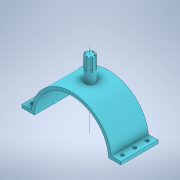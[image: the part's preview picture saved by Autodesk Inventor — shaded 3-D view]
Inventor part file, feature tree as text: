
AUTODESK INVENTOR PART (.ipt)
format: ipt  version: 2021 (Build 250183000, 183)  size: 183,296 bytes
history: native  units: in
note: dims shown in document units (in); Inventor stores cm internally (conversion verified against a paired STEP export)
features: sketch x4, extrude x3, hole x1, mirror x1, plane x1, pattern_circular x1
ambient origin geometry x8: Origin, YZ Plane, XZ Plane, XY Plane, X Axis, Y Axis, Z Axis, Center Point
bodies: Body1 (feature_tree)
feature tree (11):
  extrude  "Extrusion5"  Depth=0.25in
  hole  "Hole3"  [1 undecoded]
  mirror  "Mirror3"
  plane  "Work Plane7"
  extrude  "Extrusion11"  Depth=3.0in TaperAngle=0.0deg
  extrude  "Extrusion12"  Depth=1.0in
  pattern_circular  "Circular Pattern3"  [2 undecoded]
  sketch  "Sketch8"  dims[d52=6.0in d53=0.25in]
  sketch  "Sketch9"  dims[d54=0.75in d55=0.125in]
  sketch  "Sketch20"  dims[d56=0.25in d57=3.0in d58=0.0in]
  sketch  "Sketch21"  dims[d59=0.5in d60=1.1811in d62=1.0in d63=0.3937in d65=1.0in d67=0.266in d68=0.75in d69=0.438in d70=0.25in d71=0.5635in d72=1.0in d73=0.8108in d100=3.125in d101=0.75in d102=2.0in d103=0.0in d104=1.0in d105=0.0in d106=0.125in d107=0.125in d108=2.3622in d109=360.0deg d11=1.0in d12=1.0in d13=1.0in d14=0.15in d15=0.25in d16=0.375in d17=0.5635in d18=0.75in d19=0.8108in d20=0.0625in d21=0.75in d22=0.375in]
note: 3 required parameter values undecoded (feature->parameter linkage not recoverable at this tier; creation-order binding heuristic only, values carry confidence <= 0.55)
